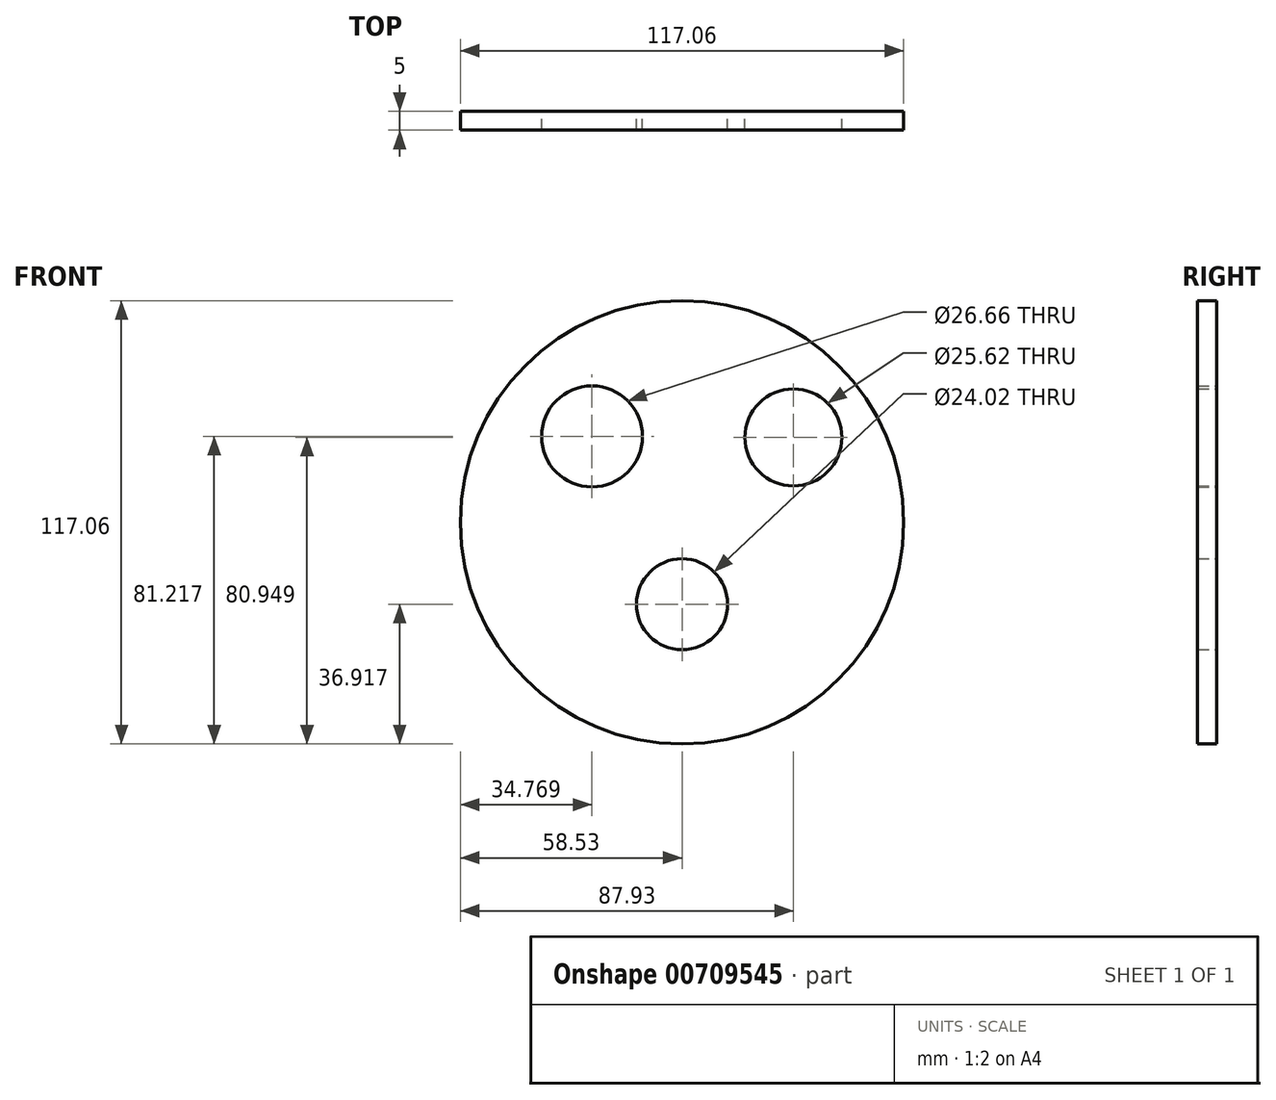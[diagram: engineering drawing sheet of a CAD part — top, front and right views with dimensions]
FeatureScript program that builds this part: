
annotation { "Feature Type Name" : "Feature", "Feature Type Description" : "" }
export const myFeature = defineFeature(function(context is Context, id is Id, definition is map)
    precondition{}
    {
        {
            var Q0;
            Q0=qCreatedBy(makeId("Front.planeOp"),FACE);
            var sketch = newSketch(context, id + "F0", { "sketchPlane" : qUnion([Q0])});
            skCircle(sketch, "E0", {"center": v(0, 0) * mm, "radius": 58.53 * mm});
            skCircle(sketch, "E1", {"center": v(-23.76, 22.69) * mm, "radius": 13.33 * mm});
            skCircle(sketch, "E2", {"center": v(29.4, 22.42) * mm, "radius": 12.8 * mm});
            skCircle(sketch, "E3", {"center": v(0, -21.61) * mm, "radius": 12.01 * mm});
            skSolve(sketch);
        }
        {
            var Q0;
            Q0=makeQuery(id+"F0.imprint","IMPRINT",FACE,{"disambiguationData":[TD([[makeQuery(id+"F0.imprint","IMPRINT",EDGE,{"derivedFrom":sQuery(id+"F0.wireOp",EDGE,"E0")}),1.0]])]});
            extrude(context, id + "F1", {"entities" : qUnion([Q0]), "depth" : 5 * mm, "offsetDistance" : 25.4 * mm});
        }
    });
